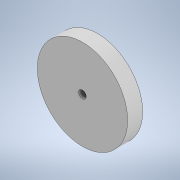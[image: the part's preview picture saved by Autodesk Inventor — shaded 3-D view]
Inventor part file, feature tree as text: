
AUTODESK INVENTOR PART (.ipt)
format: ipt  version: 2021 (Build 250183000, 183)  size: 99,328 bytes
history: native  units: mm
features: extrude x2, sketch x2
ambient origin geometry x8: Origin, YZ Plane, XZ Plane, XY Plane, X Axis, Y Axis, Z Axis, Center Point
bodies: Solid1 (feature_tree)
feature tree (4):
  extrude  "Extrusion1"  Depth=6.0mm TaperAngle=0.0deg
  extrude  "Extrusion2"  Depth=6.0mm TaperAngle=0.0deg
  sketch  "Sketch1"  dims[d0=36.0mm d1=6.0mm d2=0.0mm]
  sketch  "Sketch2"  dims[d3=3.0mm d4=6.0mm d5=0.0mm]
